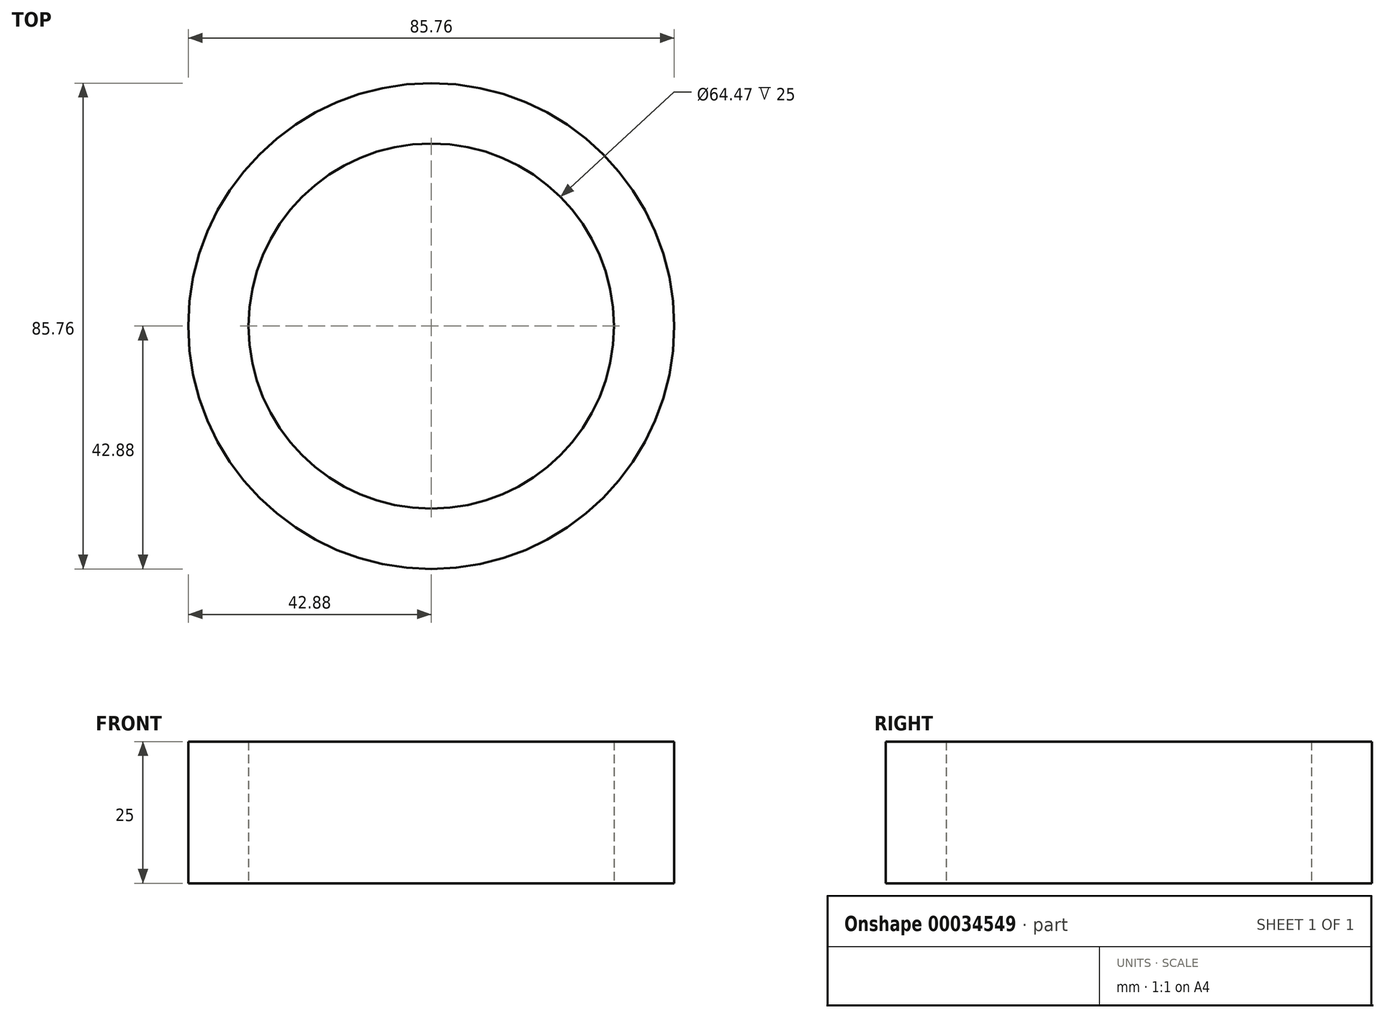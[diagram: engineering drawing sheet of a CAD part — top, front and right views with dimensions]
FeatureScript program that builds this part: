
annotation { "Feature Type Name" : "Feature", "Feature Type Description" : "" }
export const myFeature = defineFeature(function(context is Context, id is Id, definition is map)
    precondition{}
    {
        {
            var Q0;
            Q0=qCreatedBy(makeId("Top.planeOp"),FACE);
            var sketch = newSketch(context, id + "F0", { "sketchPlane" : qUnion([Q0])});
            skCircle(sketch, "E0", {"center": v(0, 0) * mm, "radius": 32.23 * mm});
            skCircle(sketch, "E1", {"center": v(0, 0) * mm, "radius": 42.88 * mm});
            skSolve(sketch);
        }
        {
            var Q0;
            Q0=makeQuery(id+"F0.imprint","IMPRINT",FACE,{"disambiguationData":[TD([[makeQuery(id+"F0.imprint","IMPRINT",EDGE,{"derivedFrom":sQuery(id+"F0.wireOp",EDGE,"E0")}),-1.0]])]});
            extrude(context, id + "F1", {"entities" : qUnion([Q0]), "depth" : 25 * mm});
        }
    });
